# Revit family: 411230001_Lavamanos sencillo cruceta Balta
name_source: partatom
category: Plumbing Fixtures
units: mm (PartAtom-declared; Revit-internal decimal feet)

## family parameters
Cut with Voids When Loaded = No
Host = Face
OmniClass Number = 23.31.11.00
OmniClass Title = Faucets
Part Type = Normal
Room Calculation Point = No
Round Connector Dimension = Use Diameter
Shared = No

## types (1)
- Lavamanos sencillo cruceta Balta
    Alto = 147 mm
    Ancho = 45 mm
    Capacidad de flujo = A 60 psi: 8.3 L/min.
    Ciclo de vida de la unidad de cierre = 500000 ciclos.
    Creado por = BIMBAU.
    Default Elevation = 0 mm  [stored 0 ft]
    Description = El LAVAMANOS SENCILLO BALTA ha sido diseñada para trabajar en perfecta armonía con el espacio; inspirada en las necesidades del consumidor latinoamericano dando como resultado un producto robusto y funcional. Ideal para instalaciones donde no se necesita mezclar agua fría y caliente. Incorpora un sistema aireador que genera un chorro de agua espumoso, agradable al tacto.
    Dimensiones generales del producto = 147 x 74 x 132 mm.
    Diámetro abasto = 13 mm  [stored 0.0426509 ft]
    Fecha de creación = 05/05/2021
    Garantía = 30 años Grival - 5 años Cromado.
    Manufacturer = Corona.
    Material = Corona_Aluminio
    Material 2 = Corona_Acero inoxidable
    Model = 411230001_Lavamanos sencillo cruceta Balta.
    Normatividad = NTC 1644.
    Peso Bruto aprox = 145 gr. / 0.32 lb.
    Peso Neto aprox = 135 gr. / 0.30 lb.
    Presión máxima recomendada = 120 psi.
    Presión mínima recomendada = 20 psi.
    Profundidad = 132 mm  [stored 0.433071 ft]
    Recubrimientos = Resistente a la corrosión, pelado y decoloración por agua. Recubrimientos no tóxicos. Producto para uso doméstico.
    Temperaturas máxima de trabajo = 71° C / 159.8° F.
    Temperaturas mínima de trabajo = 5° C / 41° F.

note: [stored X ft] marks values corroborated as IEEE doubles in the binary element streams (Revit-internal decimal feet)

## geometry (parser evidence)
native form markers: Sweep x8
no freeform markers — native parametric forms only
